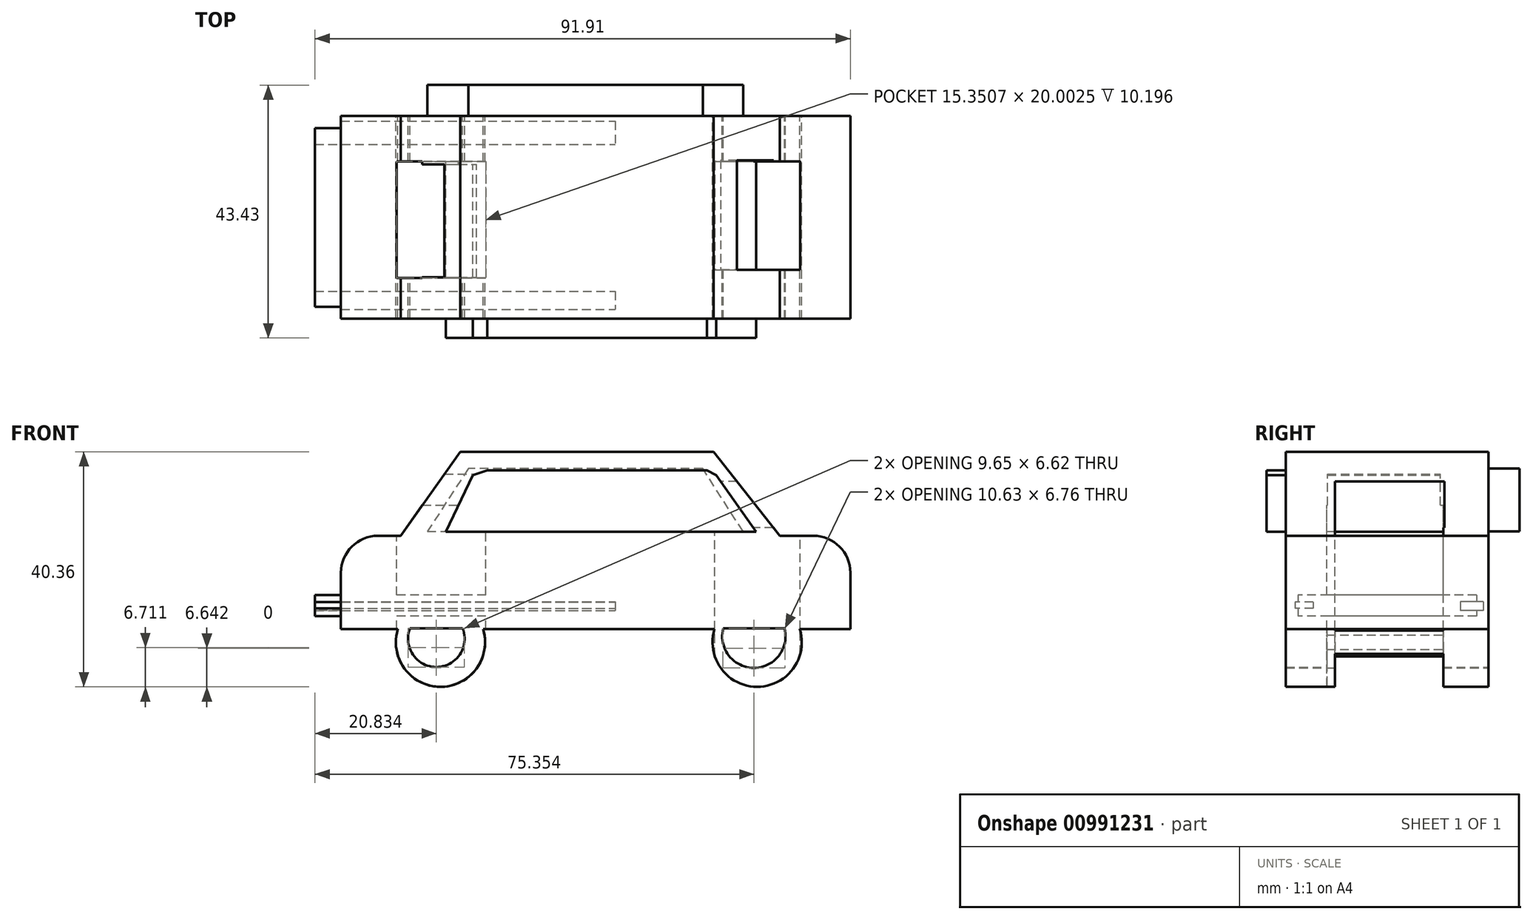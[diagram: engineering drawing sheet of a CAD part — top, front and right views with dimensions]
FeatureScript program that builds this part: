
annotation { "Feature Type Name" : "Feature", "Feature Type Description" : "" }
export const myFeature = defineFeature(function(context is Context, id is Id, definition is map)
    precondition{}
    {
        {
            var Q0;
            Q0=qCreatedBy(makeId("Front.planeOp"),FACE);
            var sketch = newSketch(context, id + "F0", { "sketchPlane" : qUnion([Q0])});
            skLineSegment(sketch, "E0.bottom", {"start": v(-40.75, -5.23) * mm, "end": v(34, -5.23) * mm});
            skLineSegment(sketch, "E0.left", {"start": v(-47.1, -11.58) * mm, "end": v(-47.1, -21.28) * mm});
            skLineSegment(sketch, "E0.right", {"start": v(40.35, -11.58) * mm, "end": v(40.35, -21.28) * mm});
            skLineSegment(sketch, "E1", {"start": v(-36.87, -5.23) * mm, "end": v(-26.63, 9.19) * mm});
            skLineSegment(sketch, "E2", {"start": v(-26.63, 9.19) * mm, "end": v(16.86, 9.19) * mm});
            skLineSegment(sketch, "E3", {"start": v(16.86, 9.19) * mm, "end": v(28.26, -5.23) * mm});
            skLineSegment(sketch, "E4", {"start": v(-47.1, -21.28) * mm, "end": v(-37.34, -21.28) * mm});
            skPoint(sketch, "E4.endSnap0", {"position": v(40.35, -15.82) * mm});
            skPoint(sketch, "E5.visualSharp", {"position": v(-47.1, -5.23) * mm});
            skArc(sketch, "E5.filletArc", {"start": v(-40.75, -5.23) * mm, "mid": v(-45.24, -7.1) * mm, "end": v(-47.1, -11.58) * mm});
            skPoint(sketch, "E6.visualSharp", {"position": v(40.35, -5.23) * mm});
            skArc(sketch, "E6.filletArc", {"start": v(40.35, -11.58) * mm, "mid": v(38.5, -7.1) * mm, "end": v(34, -5.23) * mm});
            skArc(sketch, "E7", {"start": v(-37.34, -21.28) * mm, "mid": v(-30, -31.17) * mm, "end": v(-22.68, -21.28) * mm});
            skArc(sketch, "E8.MirrorCS", {"start": v(31.68, -21.28) * mm, "mid": v(24.36, -31.17) * mm, "end": v(17.03, -21.28) * mm});
            skLineSegment(sketch, "E9.trimOffspring", {"start": v(-22.68, -21.28) * mm, "end": v(17.03, -21.28) * mm});
            skLineSegment(sketch, "E10.trimOffspring", {"start": v(31.68, -21.28) * mm, "end": v(40.35, -21.28) * mm});
            skSolve(sketch);
        }
        {
            var Q0;
            {var subQ0=sQuery(id+"F0.wireOp",EDGE,"E1");Q0=makeQuery(id+"F0.imprint","IMPRINT",FACE,{"disambiguationData":[TD([[makeQuery(id+"F0.imprint","IMPRINT",EDGE,{"derivedFrom":subQ0}),-1.0]])]});}
            var Q1;
            Q1=makeQuery(id+"F0.imprint","IMPRINT",FACE,{"disambiguationData":[TD([[makeQuery(id+"F0.imprint","IMPRINT",EDGE,{"derivedFrom":sQuery(id+"F0.wireOp",EDGE,"E0.left")}),1.0]])]});
            extrude(context, id + "F1", {"entities" : qUnion([Q0, Q1]), "depth" : 34.8 * mm, "offsetDistance" : 25.4 * mm});
        }
        {
            var Q0;
            Q0=qCreatedBy(makeId("Top.planeOp"),FACE);
            var sketch = newSketch(context, id + "F2", { "sketchPlane" : qUnion([Q0])});
            skLineSegment(sketch, "E11.bottom", {"start": v(17.1, -26.4) * mm, "end": v(31.75, -26.4) * mm});
            skLineSegment(sketch, "E11.top", {"start": v(17.1, -7.8) * mm, "end": v(31.75, -7.8) * mm});
            skLineSegment(sketch, "E11.left", {"start": v(17.1, -26.4) * mm, "end": v(17.1, -7.8) * mm});
            skLineSegment(sketch, "E11.right", {"start": v(31.75, -26.4) * mm, "end": v(31.75, -7.8) * mm});
            skLineSegment(sketch, "E12.bottom", {"start": v(-37.56, -27.8) * mm, "end": v(-22.21, -27.8) * mm});
            skLineSegment(sketch, "E12.top", {"start": v(-37.56, -7.8) * mm, "end": v(-22.21, -7.8) * mm});
            skLineSegment(sketch, "E12.left", {"start": v(-37.56, -27.8) * mm, "end": v(-37.56, -7.8) * mm});
            skLineSegment(sketch, "E12.right", {"start": v(-22.21, -27.8) * mm, "end": v(-22.21, -7.8) * mm});
            skSolve(sketch);
        }
        {
            var Q0;
            Q0 = qSketchRegion(id + "F2", true);
            extrude(context, id + "F3", {"entities" : qUnion([Q0]), "operationType" : NewBodyOperationType.REMOVE, "oppositeDirection" : true, "depth" : 33.02 * mm, "offsetDistance" : 25.4 * mm});
        }
        {
            var Q0;
            Q0=qCreatedBy(makeId("Right.planeOp"),FACE);
            var sketch = newSketch(context, id + "F4", { "sketchPlane" : qUnion([Q0])});
            skLineSegment(sketch, "E13.bottom", {"start": v(-8.26, 5.38) * mm, "end": v(-27.67, 5.38) * mm});
            skLineSegment(sketch, "E13.top", {"start": v(-8.26, -4.49) * mm, "end": v(-27.67, -4.49) * mm});
            skLineSegment(sketch, "E13.left", {"start": v(-8.26, 5.38) * mm, "end": v(-8.26, -4.49) * mm});
            skLineSegment(sketch, "E13.right", {"start": v(-27.67, 5.38) * mm, "end": v(-27.67, -4.49) * mm});
            skSolve(sketch);
        }
        {
            var Q0;
            Q0 = qSketchRegion(id + "F4", true);
            extrude(context, id + "F5", {"entities" : qUnion([Q0]), "operationType" : NewBodyOperationType.REMOVE, "oppositeDirection" : true, "depth" : 230.12 * mm, "offsetDistance" : 25.4 * mm});
        }
        {
            var Q0;
            Q0=qCreatedBy(makeId("Right.planeOp"),FACE);
            var sketch = newSketch(context, id + "F6", { "sketchPlane" : qUnion([Q0])});
            skLineSegment(sketch, "E14.bottom", {"start": v(-26.4, 4.07) * mm, "end": v(-7.56, 4.07) * mm});
            skLineSegment(sketch, "E14.top", {"start": v(-26.4, -3.84) * mm, "end": v(-7.56, -3.84) * mm});
            skLineSegment(sketch, "E14.left", {"start": v(-26.4, 4.07) * mm, "end": v(-26.4, -3.84) * mm});
            skLineSegment(sketch, "E14.right", {"start": v(-7.56, 4.07) * mm, "end": v(-7.56, -3.84) * mm});
            skSolve(sketch);
        }
        {
            var Q0;
            Q0 = qSketchRegion(id + "F6", true);
            extrude(context, id + "F7", {"entities" : qUnion([Q0]), "operationType" : NewBodyOperationType.REMOVE, "depth" : 125.48 * mm, "offsetDistance" : 25.4 * mm});
        }
        {
            var Q0;
            Q0=qCreatedBy(makeId("Front.planeOp"),FACE);
            var sketch = newSketch(context, id + "F8", { "sketchPlane" : qUnion([Q0])});
            skLineSegment(sketch, "E15", {"start": v(29.06, -21.15) * mm, "end": v(18.53, -21.15) * mm});
            skArc(sketch, "E16", {"start": v(18.53, -21.15) * mm, "mid": v(23.8, -27.9) * mm, "end": v(29.06, -21.15) * mm});
            skArc(sketch, "E17", {"start": v(-35.25, -21.15) * mm, "mid": v(-30.73, -27.77) * mm, "end": v(-26.2, -21.15) * mm});
            skLineSegment(sketch, "E18.trimOffspring", {"start": v(-26.2, -21.15) * mm, "end": v(-35.25, -21.15) * mm});
            skSolve(sketch);
        }
        {
            var Q0;
            Q0=makeQuery(id+"F8.imprint","IMPRINT",FACE,{"disambiguationData":[TD([[makeQuery(id+"F8.imprint","IMPRINT",EDGE,{"derivedFrom":sQuery(id+"F8.wireOp",EDGE,"E17")}),1.0]])]});
            var Q1;
            Q1=makeQuery(id+"F8.imprint","IMPRINT",FACE,{"disambiguationData":[TD([[makeQuery(id+"F8.imprint","IMPRINT",EDGE,{"derivedFrom":sQuery(id+"F8.wireOp",EDGE,"E15")}),1.0]])]});
            extrude(context, id + "F9", {"entities" : qUnion([Q0, Q1]), "operationType" : NewBodyOperationType.REMOVE, "depth" : 83.57 * mm, "offsetDistance" : 25.4 * mm});
        }
        {
            var Q0;
            Q0=qCreatedBy(makeId("Front.planeOp"),FACE);
            var sketch = newSketch(context, id + "F10", { "sketchPlane" : qUnion([Q0])});
            skLineSegment(sketch, "E19", {"start": v(-29.08, -4.53) * mm, "end": v(24.2, -4.53) * mm});
            skLineSegment(sketch, "E20", {"start": v(24.2, -4.53) * mm, "end": v(17.3, 5.17) * mm});
            skLineSegment(sketch, "E21", {"start": v(17.3, 5.17) * mm, "end": v(15.74, 6) * mm});
            skLineSegment(sketch, "E22", {"start": v(15.74, 6) * mm, "end": v(-22, 6) * mm});
            skLineSegment(sketch, "E23", {"start": v(-22, 6) * mm, "end": v(-24.47, 5.17) * mm});
            skLineSegment(sketch, "E24", {"start": v(-24.47, 5.17) * mm, "end": v(-29.08, -4.53) * mm});
            skSolve(sketch);
        }
        {
            var Q0;
            Q0 = qSketchRegion(id + "F10", true);
            extrude(context, id + "F11", {"entities" : qUnion([Q0]), "operationType" : NewBodyOperationType.ADD, "depth" : 38.1 * mm, "offsetDistance" : 25.4 * mm});
        }
        {
            var Q0;
            Q0=qCreatedBy(makeId("Front.planeOp"),FACE);
            var sketch = newSketch(context, id + "F12", { "sketchPlane" : qUnion([Q0])});
            skLineSegment(sketch, "E25", {"start": v(15.02, 6.28) * mm, "end": v(-25.23, 6.28) * mm});
            skLineSegment(sketch, "E26", {"start": v(-25.23, 6.28) * mm, "end": v(-32.28, -4.5) * mm});
            skLineSegment(sketch, "E27", {"start": v(-32.28, -4.5) * mm, "end": v(21.93, -4.5) * mm});
            skLineSegment(sketch, "E28", {"start": v(21.93, -4.5) * mm, "end": v(15.02, 6.28) * mm});
            skSolve(sketch);
        }
        {
            var Q0;
            Q0 = qSketchRegion(id + "F12", true);
            extrude(context, id + "F13", {"entities" : qUnion([Q0]), "operationType" : NewBodyOperationType.ADD, "oppositeDirection" : true, "depth" : 5.33 * mm, "offsetDistance" : 25.4 * mm});
        }
        {
            var Q0;
            Q0=qCreatedBy(makeId("Right.planeOp"),FACE);
            var sketch = newSketch(context, id + "F14", { "sketchPlane" : qUnion([Q0])});
            skLineSegment(sketch, "E29.bottom", {"start": v(-2.04, -15.43) * mm, "end": v(-32.74, -15.43) * mm});
            skLineSegment(sketch, "E29.top", {"start": v(-2.04, -19.03) * mm, "end": v(-32.74, -19.03) * mm});
            skLineSegment(sketch, "E29.left", {"start": v(-2.04, -15.43) * mm, "end": v(-2.04, -19.03) * mm});
            skLineSegment(sketch, "E29.right", {"start": v(-32.74, -15.43) * mm, "end": v(-32.74, -19.03) * mm});
            skSolve(sketch);
        }
        {
            var Q0;
            Q0 = qSketchRegion(id + "F14", true);
            extrude(context, id + "F15", {"entities" : qUnion([Q0]), "operationType" : NewBodyOperationType.ADD, "oppositeDirection" : true, "depth" : 51.56 * mm, "offsetDistance" : 25.4 * mm});
        }
        {
            var Q0;
            Q0=qCreatedBy(makeId("Right.planeOp"),FACE);
            var sketch = newSketch(context, id + "F16", { "sketchPlane" : qUnion([Q0])});
            skLineSegment(sketch, "E30.bottom", {"start": v(-0.88, -16.55) * mm, "end": v(-4.87, -16.55) * mm});
            skLineSegment(sketch, "E30.top", {"start": v(-0.88, -18.1) * mm, "end": v(-4.87, -18.1) * mm});
            skLineSegment(sketch, "E30.left", {"start": v(-0.88, -16.55) * mm, "end": v(-0.88, -18.1) * mm});
            skLineSegment(sketch, "E30.right", {"start": v(-4.87, -16.55) * mm, "end": v(-4.87, -18.1) * mm});
            skSolve(sketch);
        }
        {
            var Q0;
            Q0 = qSketchRegion(id + "F16", true);
            extrude(context, id + "F17", {"entities" : qUnion([Q0]), "operationType" : NewBodyOperationType.REMOVE, "oppositeDirection" : true, "depth" : 90.93 * mm, "offsetDistance" : 25.4 * mm});
        }
        {
            var Q0;
            Q0=qCreatedBy(makeId("Right.planeOp"),FACE);
            var sketch = newSketch(context, id + "F18", { "sketchPlane" : qUnion([Q0])});
            skLineSegment(sketch, "E31.bottom", {"start": v(-30.1, -16.61) * mm, "end": v(-33.2, -16.61) * mm});
            skLineSegment(sketch, "E31.top", {"start": v(-30.1, -17.72) * mm, "end": v(-33.2, -17.72) * mm});
            skLineSegment(sketch, "E31.left", {"start": v(-30.1, -16.61) * mm, "end": v(-30.1, -17.72) * mm});
            skLineSegment(sketch, "E31.right", {"start": v(-33.2, -16.61) * mm, "end": v(-33.2, -17.72) * mm});
            skSolve(sketch);
        }
        {
            var Q0;
            Q0 = qSketchRegion(id + "F18", true);
            extrude(context, id + "F19", {"entities" : qUnion([Q0]), "operationType" : NewBodyOperationType.REMOVE, "oppositeDirection" : true, "depth" : 112.17 * mm, "offsetDistance" : 25.4 * mm});
        }
    });
